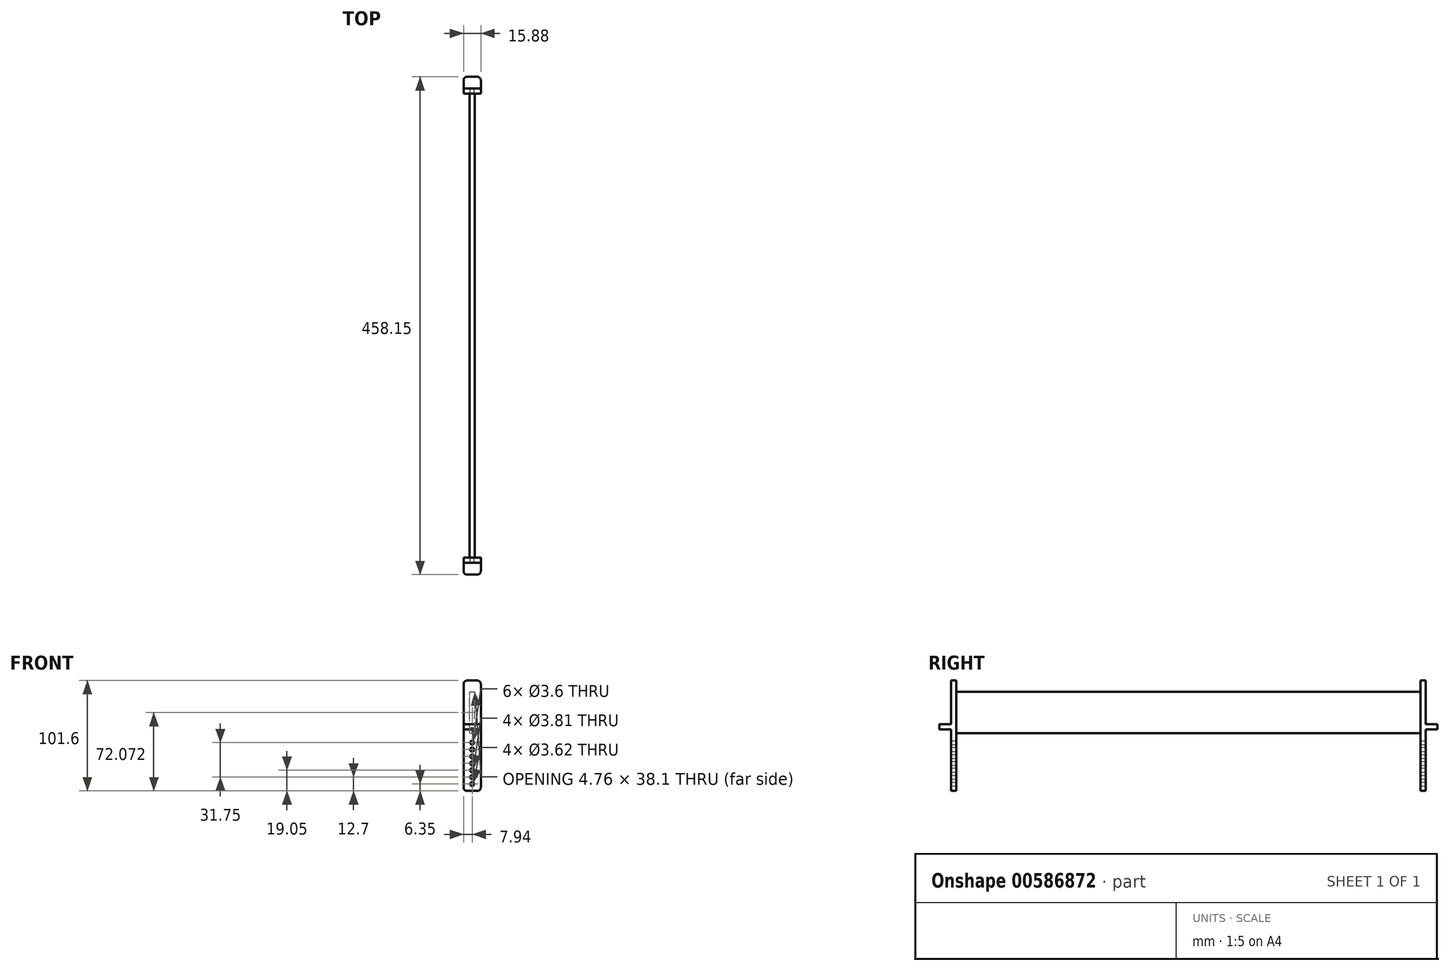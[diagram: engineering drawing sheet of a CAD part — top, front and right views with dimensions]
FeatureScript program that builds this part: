
annotation { "Feature Type Name" : "Feature", "Feature Type Description" : "" }
export const myFeature = defineFeature(function(context is Context, id is Id, definition is map)
    precondition{}
    {
        {
            var Q0;
            Q0=qCreatedBy(makeId("Front.planeOp"),FACE);
            var sketch = newSketch(context, id + "F0", { "sketchPlane" : qUnion([Q0])});
            skLineSegment(sketch, "E0.bottom", {"start": v(7.94, 50.8) * mm, "end": v(-7.94, 50.8) * mm});
            skLineSegment(sketch, "E0.top", {"start": v(7.94, -50.8) * mm, "end": v(-7.94, -50.8) * mm});
            skLineSegment(sketch, "E0.left", {"start": v(7.94, 50.8) * mm, "end": v(7.94, -50.8) * mm});
            skLineSegment(sketch, "E0.right", {"start": v(-7.94, 50.8) * mm, "end": v(-7.94, -50.8) * mm});
            skPoint(sketch, "E0.middle", {"position": v(0, 0) * mm});
            skSolve(sketch);
        }
        {
            var Q0;
            Q0=qCreatedBy(makeId("Front.planeOp"),FACE);
            var sketch = newSketch(context, id + "F1", { "sketchPlane" : qUnion([Q0])});
            skLineSegment(sketch, "E1.bottom", {"start": v(2.38, 40.32) * mm, "end": v(-2.38, 40.32) * mm});
            skLineSegment(sketch, "E1.top", {"start": v(2.38, 2.22) * mm, "end": v(-2.38, 2.22) * mm});
            skLineSegment(sketch, "E1.left", {"start": v(2.38, 40.32) * mm, "end": v(2.38, 2.22) * mm});
            skLineSegment(sketch, "E1.right", {"start": v(-2.38, 40.32) * mm, "end": v(-2.38, 2.22) * mm});
            skPoint(sketch, "E1.middle", {"position": v(0, 21.27) * mm});
            skSolve(sketch);
        }
        {
            var Q0;
            Q0=qCreatedBy(makeId("Front.planeOp"),FACE);
            var sketch = newSketch(context, id + "F2", { "sketchPlane" : qUnion([Q0])});
            skLineSegment(sketch, "E2.bottom", {"start": v(7.94, 10.67) * mm, "end": v(-7.94, 10.67) * mm});
            skLineSegment(sketch, "E2.top", {"start": v(7.94, 5.9) * mm, "end": v(-7.94, 5.9) * mm});
            skLineSegment(sketch, "E2.left", {"start": v(7.94, 10.67) * mm, "end": v(7.94, 5.9) * mm});
            skLineSegment(sketch, "E2.right", {"start": v(-7.94, 10.67) * mm, "end": v(-7.94, 5.9) * mm});
            skPoint(sketch, "E2.middle", {"position": v(0, 8.29) * mm});
            skSolve(sketch);
        }
        {
            var Q0;
            Q0=qCreatedBy(makeId("Front.planeOp"),FACE);
            var sketch = newSketch(context, id + "F3", { "sketchPlane" : qUnion([Q0])});
            skCircle(sketch, "E3", {"center": v(0, -31.75) * mm, "radius": 1.9 * mm});
            skCircle(sketch, "E4", {"center": v(0, -38.1) * mm, "radius": 1.8 * mm});
            skCircle(sketch, "E5", {"center": v(0, -44.45) * mm, "radius": 1.8 * mm});
            skCircle(sketch, "E6", {"center": v(0, -12.7) * mm, "radius": 1.9 * mm});
            skCircle(sketch, "E7", {"center": v(0, -19.05) * mm, "radius": 1.8 * mm});
            skCircle(sketch, "E8", {"center": v(0, -25.4) * mm, "radius": 1.8 * mm});
            skCircle(sketch, "E9", {"center": v(0, -6.35) * mm, "radius": 1.8 * mm});
            skSolve(sketch);
        }
        {
            var Q0;
            Q0=makeQuery(id+"F0.imprint","IMPRINT",FACE,{"disambiguationData":[TD([[makeQuery(id+"F0.imprint","IMPRINT",EDGE,{"derivedFrom":sQuery(id+"F0.wireOp",EDGE,"E0.bottom")}),1.0]])]});
            extrude(context, id + "F4", {"entities" : qUnion([Q0]), "depth" : 4.76 * mm, "offsetDistance" : 25.4 * mm});
        }
        {
            var Q0;
            Q0=makeQuery(id+"F2.imprint","IMPRINT",FACE,{"disambiguationData":[TD([[makeQuery(id+"F2.imprint","IMPRINT",EDGE,{"derivedFrom":sQuery(id+"F2.wireOp",EDGE,"E2.bottom")}),1.0]])]});
            extrude(context, id + "F5", {"entities" : qUnion([Q0]), "operationType" : NewBodyOperationType.ADD, "oppositeDirection" : true, "depth" : 10.8 * mm, "offsetDistance" : 25.4 * mm});
        }
        {
            var Q0;
            Q0=makeQuery(id+"F1.imprint","IMPRINT",FACE,{"disambiguationData":[TD([[makeQuery(id+"F1.imprint","IMPRINT",EDGE,{"derivedFrom":sQuery(id+"F1.wireOp",EDGE,"E1.bottom")}),1.0]])]});
            extrude(context, id + "F6", {"entities" : qUnion([Q0]), "operationType" : NewBodyOperationType.ADD, "depth" : 431.8 * mm, "offsetDistance" : 25.4 * mm});
        }
        {
            var Q0;
            Q0 = qSketchRegion(id + "F0", true);
            var Q1;
            Q1=makeQuery(id+"F6.opExtrude","CAP_FACE",FACE,{"disambiguationData":[OSD([sQuery(id+"F1.wireOp",EDGE,"E1.bottom"),sQuery(id+"F1.wireOp",EDGE,"E1.top"),sQuery(id+"F1.wireOp",EDGE,"E1.left"),sQuery(id+"F1.wireOp",EDGE,"E1.right")])],"isStart":false});
            extrude(context, id + "F7", {"entities" : qUnion([Q0]), "operationType" : NewBodyOperationType.ADD, "depth" : 436.56 * mm, "offsetDistance" : 25.4 * mm, "hasSecondDirection" : true, "secondDirectionBound" : SecondDirectionBoundingType.UP_TO_SURFACE, "secondDirectionOppositeDirection" : false, "secondDirectionDepth" : 422.15 * mm, "secondDirectionBoundEntityFace" : qUnion([Q1])});
        }
        {
            var Q0;
            Q0 = qSketchRegion(id + "F2", true);
            var Q1;
            Q1=makeQuery(id+"F7.opExtrude","CAP_FACE",FACE,{"disambiguationData":[OSD([sQuery(id+"F0.wireOp",EDGE,"E0.bottom"),sQuery(id+"F0.wireOp",EDGE,"E0.top"),sQuery(id+"F0.wireOp",EDGE,"E0.left"),sQuery(id+"F0.wireOp",EDGE,"E0.right")])],"isStart":false});
            extrude(context, id + "F8", {"entities" : qUnion([Q0]), "operationType" : NewBodyOperationType.ADD, "depth" : 447.36 * mm, "offsetDistance" : 25.4 * mm, "hasSecondDirection" : true, "secondDirectionBound" : SecondDirectionBoundingType.UP_TO_SURFACE, "secondDirectionOppositeDirection" : false, "secondDirectionDepth" : 25.4 * mm, "secondDirectionBoundEntityFace" : qUnion([Q1])});
        }
        {
            var Q0;
            Q0 = qSketchRegion(id + "F3", true);
            extrude(context, id + "F9", {"entities" : qUnion([Q0]), "operationType" : NewBodyOperationType.REMOVE, "endBound" : BoundingType.THROUGH_ALL, "depth" : 25.4 * mm, "offsetDistance" : 25.4 * mm});
        }
        {
            var Q0;
            Q0=makeQuery(id+"F6.opExtrude","SWEPT_FACE",FACE,{"disambiguationData":[OSD([sQuery(id+"F1.wireOp",EDGE,"E1.right")])]});
            var sketch = newSketch(context, id + "F10", { "sketchPlane" : qUnion([Q0])});
            skLineSegment(sketch, "E10", {"start": v(4.76, 21.27) * mm, "end": v(431.8, 21.27) * mm});
            skCircle(sketch, "E11", {"center": v(30.16, 21.27) * mm, "radius": 12.7 * mm});
            skCircle(sketch, "E12", {"center": v(68.26, 21.27) * mm, "radius": 12.7 * mm});
            skCircle(sketch, "E13", {"center": v(106.36, 21.27) * mm, "radius": 12.7 * mm});
            skCircle(sketch, "E14", {"center": v(144.46, 21.27) * mm, "radius": 12.7 * mm});
            skCircle(sketch, "E15", {"center": v(182.56, 21.27) * mm, "radius": 12.7 * mm});
            skCircle(sketch, "E16", {"center": v(254, 21.27) * mm, "radius": 12.7 * mm});
            skCircle(sketch, "E17", {"center": v(292.1, 21.27) * mm, "radius": 12.7 * mm});
            skCircle(sketch, "E18", {"center": v(330.2, 21.27) * mm, "radius": 12.7 * mm});
            skCircle(sketch, "E19", {"center": v(368.3, 21.27) * mm, "radius": 12.7 * mm});
            skCircle(sketch, "E20", {"center": v(406.4, 21.27) * mm, "radius": 12.7 * mm});
            skLineSegment(sketch, "E21.bottom", {"start": v(431.8, 40.32) * mm, "end": v(4.76, 40.32) * mm});
            skLineSegment(sketch, "E21.top", {"start": v(431.8, 2.22) * mm, "end": v(4.76, 2.22) * mm});
            skLineSegment(sketch, "E21.left", {"start": v(431.8, 40.32) * mm, "end": v(431.8, 2.22) * mm});
            skLineSegment(sketch, "E21.right", {"start": v(4.76, 40.32) * mm, "end": v(4.76, 2.22) * mm});
            skLineSegment(sketch, "E22.bottom", {"start": v(4.76, 50.8) * mm, "end": v(0, 50.8) * mm});
            skLineSegment(sketch, "E22.top", {"start": v(4.76, -50.8) * mm, "end": v(0, -50.8) * mm});
            skLineSegment(sketch, "E22.left", {"start": v(4.76, 50.8) * mm, "end": v(4.76, -50.8) * mm});
            skLineSegment(sketch, "E22.right", {"start": v(0, 50.8) * mm, "end": v(0, -50.8) * mm});
            skLineSegment(sketch, "E23.bottom", {"start": v(0, 10.67) * mm, "end": v(-10.8, 10.67) * mm});
            skLineSegment(sketch, "E23.top", {"start": v(0, 5.9) * mm, "end": v(-10.8, 5.9) * mm});
            skLineSegment(sketch, "E23.left", {"start": v(0, 10.67) * mm, "end": v(0, 5.9) * mm});
            skLineSegment(sketch, "E23.right", {"start": v(-10.8, 10.67) * mm, "end": v(-10.8, 5.9) * mm});
            skLineSegment(sketch, "E24.bottom", {"start": v(436.56, 50.8) * mm, "end": v(431.8, 50.8) * mm});
            skLineSegment(sketch, "E24.top", {"start": v(436.56, -50.8) * mm, "end": v(431.8, -50.8) * mm});
            skLineSegment(sketch, "E24.left", {"start": v(436.56, 50.8) * mm, "end": v(436.56, -50.8) * mm});
            skLineSegment(sketch, "E24.right", {"start": v(431.8, 50.8) * mm, "end": v(431.8, -50.8) * mm});
            skLineSegment(sketch, "E25.bottom", {"start": v(436.56, 10.67) * mm, "end": v(447.36, 10.67) * mm});
            skLineSegment(sketch, "E25.top", {"start": v(436.56, 5.9) * mm, "end": v(447.36, 5.9) * mm});
            skLineSegment(sketch, "E25.left", {"start": v(436.56, 10.67) * mm, "end": v(436.56, 5.9) * mm});
            skLineSegment(sketch, "E25.right", {"start": v(447.36, 10.67) * mm, "end": v(447.36, 5.9) * mm});
            skSolve(sketch);
        }
        {
            var Q0;
            Q0=makeQuery(id+"F6.opExtrude","SWEPT_EDGE",EDGE,{"disambiguationData":[OSD([sQuery(id+"F1.wireOp",EDGE,"E1.bottom"),sQuery(id+"F1.wireOp",EDGE,"E1.right")])]});
            var Q1;
            Q1=makeQuery(id+"F6.opExtrude","SWEPT_EDGE",EDGE,{"disambiguationData":[OSD([sQuery(id+"F1.wireOp",EDGE,"E1.bottom"),sQuery(id+"F1.wireOp",EDGE,"E1.left")])]});
            var Q2;
            Q2=makeQuery(id+"F6.opExtrude","SWEPT_EDGE",EDGE,{"disambiguationData":[OSD([sQuery(id+"F1.wireOp",EDGE,"E1.top"),sQuery(id+"F1.wireOp",EDGE,"E1.left")])]});
            var Q3;
            Q3=makeQuery(id+"F6.opExtrude","SWEPT_EDGE",EDGE,{"disambiguationData":[OSD([sQuery(id+"F1.wireOp",EDGE,"E1.top"),sQuery(id+"F1.wireOp",EDGE,"E1.right")])]});
            fillet(context, id + "F11", {"entities" : qUnion([Q0, Q1, Q2, Q3]), "radius" : 1.59 * mm, "tangentPropagation" : true, "allowEdgeOverflow" : false});
        }
        {
            var Q0;
            Q0=makeQuery(id+"F7.opExtrude","SWEPT_EDGE",EDGE,{"disambiguationData":[OSD([sQuery(id+"F0.wireOp",EDGE,"E0.bottom"),sQuery(id+"F0.wireOp",EDGE,"E0.left")])]});
            var Q1;
            Q1=makeQuery(id+"F7.opExtrude","SWEPT_EDGE",EDGE,{"disambiguationData":[OSD([sQuery(id+"F0.wireOp",EDGE,"E0.bottom"),sQuery(id+"F0.wireOp",EDGE,"E0.right")])]});
            var Q2;
            Q2=makeQuery(id+"F7.opExtrude","SWEPT_EDGE",EDGE,{"disambiguationData":[OSD([sQuery(id+"F0.wireOp",EDGE,"E0.top"),sQuery(id+"F0.wireOp",EDGE,"E0.left")])]});
            var Q3;
            Q3=makeQuery(id+"F7.opExtrude","SWEPT_EDGE",EDGE,{"disambiguationData":[OSD([sQuery(id+"F0.wireOp",EDGE,"E0.top"),sQuery(id+"F0.wireOp",EDGE,"E0.right")])]});
            var Q4;
            Q4=makeQuery(id+"F8.opExtrude","CAP_EDGE",EDGE,{"disambiguationData":[OSD([sQuery(id+"F2.wireOp",EDGE,"E2.right")])],"isStart":false});
            var Q5;
            Q5=makeQuery(id+"F8.opExtrude","CAP_EDGE",EDGE,{"disambiguationData":[OSD([sQuery(id+"F2.wireOp",EDGE,"E2.left")])],"isStart":false});
            var Q6;
            Q6=makeQuery(id+"F4.opExtrude","SWEPT_EDGE",EDGE,{"disambiguationData":[OSD([sQuery(id+"F0.wireOp",EDGE,"E0.bottom"),sQuery(id+"F0.wireOp",EDGE,"E0.left")])]});
            var Q7;
            Q7=makeQuery(id+"F4.opExtrude","SWEPT_EDGE",EDGE,{"disambiguationData":[OSD([sQuery(id+"F0.wireOp",EDGE,"E0.bottom"),sQuery(id+"F0.wireOp",EDGE,"E0.right")])]});
            var Q8;
            Q8=makeQuery(id+"F4.opExtrude","SWEPT_EDGE",EDGE,{"disambiguationData":[OSD([sQuery(id+"F0.wireOp",EDGE,"E0.top"),sQuery(id+"F0.wireOp",EDGE,"E0.left")])]});
            var Q9;
            Q9=makeQuery(id+"F4.opExtrude","SWEPT_EDGE",EDGE,{"disambiguationData":[OSD([sQuery(id+"F0.wireOp",EDGE,"E0.top"),sQuery(id+"F0.wireOp",EDGE,"E0.right")])]});
            var Q10;
            Q10=makeQuery(id+"F5.opExtrude","CAP_EDGE",EDGE,{"disambiguationData":[OSD([sQuery(id+"F2.wireOp",EDGE,"E2.right")])],"isStart":false});
            var Q11;
            Q11=makeQuery(id+"F5.opExtrude","CAP_EDGE",EDGE,{"disambiguationData":[OSD([sQuery(id+"F2.wireOp",EDGE,"E2.left")])],"isStart":false});
            fillet(context, id + "F12", {"entities" : qUnion([Q0, Q1, Q2, Q3, Q4, Q5, Q6, Q7, Q8, Q9, Q10, Q11]), "radius" : 3.17 * mm, "tangentPropagation" : true, "allowEdgeOverflow" : false});
        }
    });
